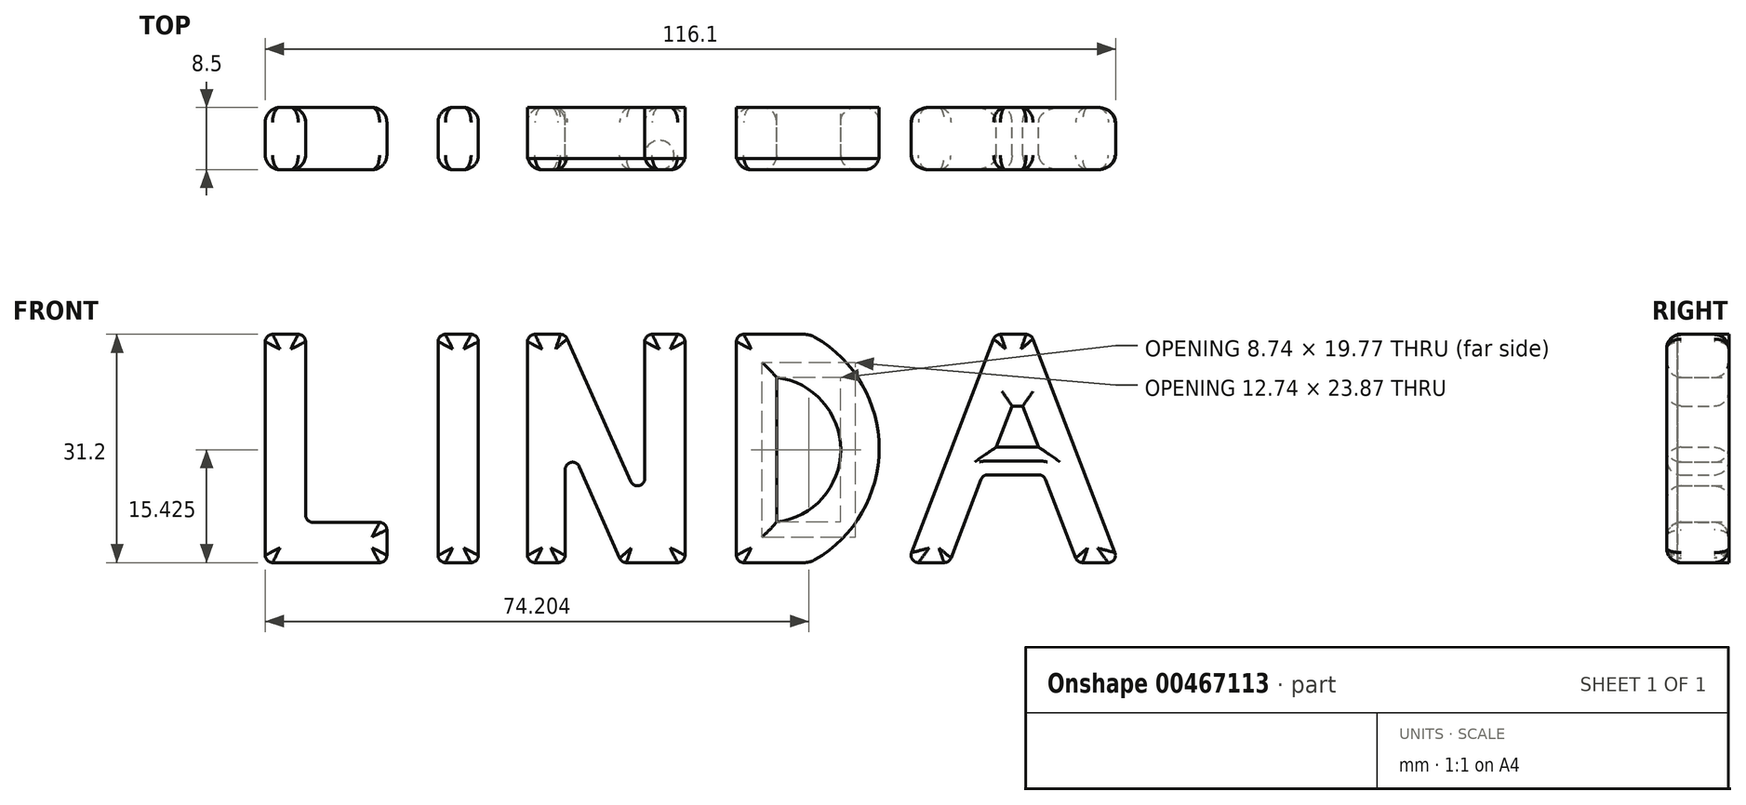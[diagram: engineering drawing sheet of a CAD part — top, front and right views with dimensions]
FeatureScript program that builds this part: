
annotation { "Feature Type Name" : "Feature", "Feature Type Description" : "" }
export const myFeature = defineFeature(function(context is Context, id is Id, definition is map)
    precondition{}
    {
        {
            var Q0;
            Q0=qCreatedBy(makeId("Front.planeOp"),FACE);
            var sketch = newSketch(context, id + "F0", { "sketchPlane" : qUnion([Q0])});
            skLineSegment(sketch, "E0", {"start": v(-68.44, 30.2) * mm, "end": v(-68.44, 1) * mm});
            skLineSegment(sketch, "E1", {"start": v(-67.44, 0) * mm, "end": v(-52.84, 0) * mm});
            skLineSegment(sketch, "E2", {"start": v(-51.84, 1) * mm, "end": v(-51.84, 4.5) * mm});
            skLineSegment(sketch, "E3", {"start": v(-52.84, 5.5) * mm, "end": v(-61.94, 5.5) * mm});
            skLineSegment(sketch, "E4", {"start": v(-62.94, 6.5) * mm, "end": v(-62.94, 30.2) * mm});
            skLineSegment(sketch, "E5", {"start": v(-63.94, 31.2) * mm, "end": v(-67.44, 31.2) * mm});
            skPoint(sketch, "E6.visualSharp", {"position": v(-62.94, 31.2) * mm});
            skArc(sketch, "E6.filletArc", {"start": v(-62.94, 30.2) * mm, "mid": v(-63.24, 30.9) * mm, "end": v(-63.94, 31.2) * mm});
            skPoint(sketch, "E7.visualSharp", {"position": v(-68.44, 31.2) * mm});
            skArc(sketch, "E7.filletArc", {"start": v(-67.44, 31.2) * mm, "mid": v(-68.15, 30.9) * mm, "end": v(-68.44, 30.2) * mm});
            skPoint(sketch, "E8.visualSharp", {"position": v(-68.44, 0) * mm});
            skArc(sketch, "E8.filletArc", {"start": v(-68.44, 1) * mm, "mid": v(-68.15, 0.3) * mm, "end": v(-67.44, 0) * mm});
            skPoint(sketch, "E9.visualSharp", {"position": v(-62.94, 5.5) * mm});
            skArc(sketch, "E9.filletArc", {"start": v(-62.94, 6.5) * mm, "mid": v(-62.65, 5.8) * mm, "end": v(-61.94, 5.5) * mm});
            skPoint(sketch, "E10.visualSharp", {"position": v(-51.84, 5.5) * mm});
            skArc(sketch, "E10.filletArc", {"start": v(-51.84, 4.5) * mm, "mid": v(-52.13, 5.2) * mm, "end": v(-52.84, 5.5) * mm});
            skPoint(sketch, "E11.visualSharp", {"position": v(-51.84, 0) * mm});
            skArc(sketch, "E11.filletArc", {"start": v(-52.84, 0) * mm, "mid": v(-52.13, 0.3) * mm, "end": v(-51.84, 1) * mm});
            skLineSegment(sketch, "E12", {"start": v(19.81, 1.36) * mm, "end": v(31.02, 30.55) * mm});
            skLineSegment(sketch, "E13", {"start": v(31.95, 31.2) * mm, "end": v(35.45, 31.2) * mm});
            skLineSegment(sketch, "E14", {"start": v(36.39, 30.55) * mm, "end": v(47.6, 1.36) * mm});
            skLineSegment(sketch, "E15", {"start": v(46.66, 0) * mm, "end": v(43.16, 0) * mm});
            skLineSegment(sketch, "E16", {"start": v(42.23, 0.64) * mm, "end": v(38.11, 11.36) * mm});
            skLineSegment(sketch, "E17", {"start": v(37.18, 12) * mm, "end": v(30.23, 12) * mm});
            skLineSegment(sketch, "E18", {"start": v(29.3, 11.36) * mm, "end": v(25.18, 0.64) * mm});
            skLineSegment(sketch, "E19", {"start": v(24.25, 0) * mm, "end": v(20.75, 0) * mm});
            skPoint(sketch, "E20.visualSharp", {"position": v(31.27, 31.2) * mm});
            skArc(sketch, "E20.filletArc", {"start": v(31.95, 31.2) * mm, "mid": v(31.39, 31.02) * mm, "end": v(31.02, 30.55) * mm});
            skPoint(sketch, "E21.visualSharp", {"position": v(19.3, 0) * mm});
            skArc(sketch, "E21.filletArc", {"start": v(19.81, 1.36) * mm, "mid": v(19.92, 0.43) * mm, "end": v(20.75, 0) * mm});
            skPoint(sketch, "E22.visualSharp", {"position": v(24.94, 0) * mm});
            skArc(sketch, "E22.filletArc", {"start": v(24.25, 0) * mm, "mid": v(24.81, 0.18) * mm, "end": v(25.18, 0.64) * mm});
            skPoint(sketch, "E23.visualSharp", {"position": v(29.54, 12) * mm});
            skArc(sketch, "E23.filletArc", {"start": v(30.23, 12) * mm, "mid": v(29.66, 11.83) * mm, "end": v(29.3, 11.36) * mm});
            skPoint(sketch, "E24.visualSharp", {"position": v(37.87, 12) * mm});
            skArc(sketch, "E24.filletArc", {"start": v(38.11, 11.36) * mm, "mid": v(37.75, 11.83) * mm, "end": v(37.18, 12) * mm});
            skPoint(sketch, "E25.visualSharp", {"position": v(42.47, 0) * mm});
            skArc(sketch, "E25.filletArc", {"start": v(42.23, 0.64) * mm, "mid": v(42.6, 0.18) * mm, "end": v(43.16, 0) * mm});
            skPoint(sketch, "E26.visualSharp", {"position": v(48.12, 0) * mm});
            skArc(sketch, "E26.filletArc", {"start": v(46.66, 0) * mm, "mid": v(47.49, 0.43) * mm, "end": v(47.6, 1.36) * mm});
            skPoint(sketch, "E27.visualSharp", {"position": v(36.14, 31.2) * mm});
            skArc(sketch, "E27.filletArc", {"start": v(36.39, 30.55) * mm, "mid": v(36.02, 31.02) * mm, "end": v(35.45, 31.2) * mm});
            skLineSegment(sketch, "E28", {"start": v(31.36, 15.77) * mm, "end": v(33.53, 21.4) * mm});
            skLineSegment(sketch, "E29", {"start": v(33.53, 21.4) * mm, "end": v(35.02, 21.4) * mm});
            skLineSegment(sketch, "E30", {"start": v(35.02, 21.4) * mm, "end": v(37.18, 15.77) * mm});
            skLineSegment(sketch, "E31", {"start": v(37.18, 15.77) * mm, "end": v(31.36, 15.77) * mm});
            skLineSegment(sketch, "E32", {"start": v(-43.84, 0) * mm, "end": v(-40.34, 0) * mm});
            skLineSegment(sketch, "E33", {"start": v(-39.34, 1) * mm, "end": v(-39.34, 30.2) * mm});
            skLineSegment(sketch, "E34", {"start": v(-40.34, 31.2) * mm, "end": v(-43.84, 31.2) * mm});
            skLineSegment(sketch, "E35", {"start": v(-44.84, 30.2) * mm, "end": v(-44.84, 1) * mm});
            skLineSegment(sketch, "E36", {"start": v(-31.63, 0) * mm, "end": v(-28.48, 0) * mm});
            skLineSegment(sketch, "E37", {"start": v(-32.63, 1) * mm, "end": v(-32.63, 30.2) * mm});
            skLineSegment(sketch, "E38", {"start": v(-31.63, 31.2) * mm, "end": v(-28.13, 31.2) * mm});
            skLineSegment(sketch, "E39", {"start": v(-27.22, 30.6) * mm, "end": v(-18.54, 11.1) * mm});
            skLineSegment(sketch, "E40", {"start": v(-27.48, 1) * mm, "end": v(-27.48, 12.73) * mm});
            skLineSegment(sketch, "E41", {"start": v(-25.57, 13.13) * mm, "end": v(-20.04, 0.6) * mm});
            skLineSegment(sketch, "E42", {"start": v(-19.13, 0) * mm, "end": v(-12.13, 0) * mm});
            skLineSegment(sketch, "E43", {"start": v(-11.13, 1) * mm, "end": v(-11.13, 30.2) * mm});
            skLineSegment(sketch, "E44", {"start": v(-12.13, 31.2) * mm, "end": v(-15.63, 31.2) * mm});
            skLineSegment(sketch, "E45", {"start": v(-16.63, 30.2) * mm, "end": v(-16.63, 11.5) * mm});
            skPoint(sketch, "E46.visualSharp", {"position": v(-32.63, 31.2) * mm});
            skArc(sketch, "E46.filletArc", {"start": v(-31.63, 31.2) * mm, "mid": v(-32.34, 30.9) * mm, "end": v(-32.63, 30.2) * mm});
            skPoint(sketch, "E47.visualSharp", {"position": v(-27.48, 31.2) * mm});
            skArc(sketch, "E47.filletArc", {"start": v(-27.22, 30.6) * mm, "mid": v(-27.59, 31.03) * mm, "end": v(-28.13, 31.2) * mm});
            skPoint(sketch, "E48.visualSharp", {"position": v(-16.63, 6.79) * mm});
            skArc(sketch, "E48.filletArc", {"start": v(-18.54, 11.1) * mm, "mid": v(-17.42, 10.52) * mm, "end": v(-16.63, 11.5) * mm});
            skPoint(sketch, "E49.visualSharp", {"position": v(-27.48, 17.47) * mm});
            skArc(sketch, "E49.filletArc", {"start": v(-25.57, 13.13) * mm, "mid": v(-26.69, 13.7) * mm, "end": v(-27.48, 12.73) * mm});
            skPoint(sketch, "E50.visualSharp", {"position": v(-16.63, 31.2) * mm});
            skArc(sketch, "E50.filletArc", {"start": v(-15.63, 31.2) * mm, "mid": v(-16.33, 30.9) * mm, "end": v(-16.63, 30.2) * mm});
            skPoint(sketch, "E51.visualSharp", {"position": v(-11.13, 31.2) * mm});
            skArc(sketch, "E51.filletArc", {"start": v(-11.13, 30.2) * mm, "mid": v(-11.42, 30.9) * mm, "end": v(-12.13, 31.2) * mm});
            skPoint(sketch, "E52.visualSharp", {"position": v(-11.13, 0) * mm});
            skArc(sketch, "E52.filletArc", {"start": v(-12.13, 0) * mm, "mid": v(-11.42, 0.3) * mm, "end": v(-11.13, 1) * mm});
            skPoint(sketch, "E53.visualSharp", {"position": v(-19.78, 0) * mm});
            skArc(sketch, "E53.filletArc", {"start": v(-20.04, 0.6) * mm, "mid": v(-19.67, 0.16) * mm, "end": v(-19.13, 0) * mm});
            skPoint(sketch, "E54.visualSharp", {"position": v(-27.48, 0) * mm});
            skArc(sketch, "E54.filletArc", {"start": v(-28.48, 0) * mm, "mid": v(-27.78, 0.3) * mm, "end": v(-27.48, 1) * mm});
            skPoint(sketch, "E55.visualSharp", {"position": v(-32.63, 0) * mm});
            skArc(sketch, "E55.filletArc", {"start": v(-32.63, 1) * mm, "mid": v(-32.34, 0.3) * mm, "end": v(-31.63, 0) * mm});
            skPoint(sketch, "E56.visualSharp", {"position": v(-39.34, 0) * mm});
            skArc(sketch, "E56.filletArc", {"start": v(-40.34, 0) * mm, "mid": v(-39.63, 0.3) * mm, "end": v(-39.34, 1) * mm});
            skPoint(sketch, "E57.visualSharp", {"position": v(-39.34, 31.2) * mm});
            skArc(sketch, "E57.filletArc", {"start": v(-39.34, 30.2) * mm, "mid": v(-39.63, 30.9) * mm, "end": v(-40.34, 31.2) * mm});
            skPoint(sketch, "E58.visualSharp", {"position": v(-44.84, 31.2) * mm});
            skArc(sketch, "E58.filletArc", {"start": v(-43.84, 31.2) * mm, "mid": v(-44.55, 30.9) * mm, "end": v(-44.84, 30.2) * mm});
            skPoint(sketch, "E59.visualSharp", {"position": v(-44.84, 0) * mm});
            skArc(sketch, "E59.filletArc", {"start": v(-44.84, 1) * mm, "mid": v(-44.55, 0.3) * mm, "end": v(-43.84, 0) * mm});
            skLineSegment(sketch, "E60", {"start": v(-3.1, 0) * mm, "end": v(5.13, 0) * mm});
            skLineSegment(sketch, "E61", {"start": v(-4.1, 1) * mm, "end": v(-4.1, 30.2) * mm});
            skLineSegment(sketch, "E62", {"start": v(-3.1, 31.2) * mm, "end": v(5.13, 31.2) * mm});
            skArc(sketch, "E63", {"start": v(6.64, 0.4) * mm, "mid": v(15.38, 15.6) * mm, "end": v(6.64, 30.8) * mm});
            skLineSegment(sketch, "E64", {"start": v(1.4, 25.3) * mm, "end": v(1.4, 5.54) * mm});
            skArc(sketch, "E65", {"start": v(1.4, 5.54) * mm, "mid": v(10.13, 15.43) * mm, "end": v(1.4, 25.3) * mm});
            skPoint(sketch, "E66.visualSharp", {"position": v(-4.1, 31.2) * mm});
            skArc(sketch, "E66.filletArc", {"start": v(-3.1, 31.2) * mm, "mid": v(-3.81, 30.9) * mm, "end": v(-4.1, 30.2) * mm});
            skPoint(sketch, "E67.visualSharp", {"position": v(-4.1, 0) * mm});
            skArc(sketch, "E67.filletArc", {"start": v(-4.1, 1) * mm, "mid": v(-3.81, 0.3) * mm, "end": v(-3.1, 0) * mm});
            skPoint(sketch, "E68.visualSharp", {"position": v(5.9, 31.2) * mm});
            skArc(sketch, "E68.filletArc", {"start": v(6.64, 30.8) * mm, "mid": v(5.9, 31.1) * mm, "end": v(5.13, 31.2) * mm});
            skPoint(sketch, "E69.visualSharp", {"position": v(5.9, 0) * mm});
            skArc(sketch, "E69.filletArc", {"start": v(5.13, 0) * mm, "mid": v(5.9, 0.1) * mm, "end": v(6.64, 0.4) * mm});
            skSolve(sketch);
        }
        {
            var Q0;
            Q0 = qSketchRegion(id + "F0", true);
            extrude(context, id + "F1", {"entities" : qUnion([Q0]), "depth" : 8.5 * mm});
        }
        {
            var Q0;
            Q0=makeQuery(id+"F1.opExtrude","CAP_FACE",FACE,{"disambiguationData":[OSD([sQuery(id+"F0.wireOp",EDGE,"E0"),sQuery(id+"F0.wireOp",EDGE,"E1"),sQuery(id+"F0.wireOp",EDGE,"E2"),sQuery(id+"F0.wireOp",EDGE,"E3"),sQuery(id+"F0.wireOp",EDGE,"E4"),sQuery(id+"F0.wireOp",EDGE,"E5"),sQuery(id+"F0.wireOp",EDGE,"E6.filletArc"),sQuery(id+"F0.wireOp",EDGE,"E7.filletArc"),sQuery(id+"F0.wireOp",EDGE,"E8.filletArc"),sQuery(id+"F0.wireOp",EDGE,"E9.filletArc"),sQuery(id+"F0.wireOp",EDGE,"E10.filletArc"),sQuery(id+"F0.wireOp",EDGE,"E11.filletArc")])],"isStart":false});
            var Q1;
            Q1=makeQuery(id+"F1.opExtrude","CAP_FACE",FACE,{"disambiguationData":[OSD([sQuery(id+"F0.wireOp",EDGE,"E0"),sQuery(id+"F0.wireOp",EDGE,"E1"),sQuery(id+"F0.wireOp",EDGE,"E2"),sQuery(id+"F0.wireOp",EDGE,"E3"),sQuery(id+"F0.wireOp",EDGE,"E4"),sQuery(id+"F0.wireOp",EDGE,"E5"),sQuery(id+"F0.wireOp",EDGE,"E6.filletArc"),sQuery(id+"F0.wireOp",EDGE,"E7.filletArc"),sQuery(id+"F0.wireOp",EDGE,"E8.filletArc"),sQuery(id+"F0.wireOp",EDGE,"E9.filletArc"),sQuery(id+"F0.wireOp",EDGE,"E10.filletArc"),sQuery(id+"F0.wireOp",EDGE,"E11.filletArc")])],"isStart":true});
            fillet(context, id + "F2", {"entities" : qUnion([Q0, Q1]), "radius" : 2 * mm, "tangentPropagation" : true, "allowEdgeOverflow" : false});
        }
        {
            var Q0;
            Q0=makeQuery(id+"F0.imprint","IMPRINT",FACE,{"disambiguationData":[TD([[makeQuery(id+"F0.imprint","IMPRINT",EDGE,{"derivedFrom":sQuery(id+"F0.wireOp",EDGE,"E12")}),-1.0]])]});
            extrude(context, id + "F3", {"entities" : qUnion([Q0]), "operationType" : NewBodyOperationType.ADD, "depth" : 7 * mm});
        }
        {
            var Q0;
            Q0=makeQuery(id+"F1.opExtrude","CAP_FACE",FACE,{"disambiguationData":[OSD([sQuery(id+"F0.wireOp",EDGE,"E12"),sQuery(id+"F0.wireOp",EDGE,"E13"),sQuery(id+"F0.wireOp",EDGE,"E14"),sQuery(id+"F0.wireOp",EDGE,"E15"),sQuery(id+"F0.wireOp",EDGE,"E16"),sQuery(id+"F0.wireOp",EDGE,"E17"),sQuery(id+"F0.wireOp",EDGE,"E18"),sQuery(id+"F0.wireOp",EDGE,"E19"),sQuery(id+"F0.wireOp",EDGE,"E20.filletArc"),sQuery(id+"F0.wireOp",EDGE,"E21.filletArc"),sQuery(id+"F0.wireOp",EDGE,"E22.filletArc"),sQuery(id+"F0.wireOp",EDGE,"E23.filletArc"),sQuery(id+"F0.wireOp",EDGE,"E24.filletArc"),sQuery(id+"F0.wireOp",EDGE,"E25.filletArc"),sQuery(id+"F0.wireOp",EDGE,"E26.filletArc"),sQuery(id+"F0.wireOp",EDGE,"E27.filletArc"),sQuery(id+"F0.wireOp",EDGE,"E28"),sQuery(id+"F0.wireOp",EDGE,"E29"),sQuery(id+"F0.wireOp",EDGE,"E30"),sQuery(id+"F0.wireOp",EDGE,"E31")])],"isStart":false});
            var Q1;
            Q1=makeQuery(id+"F1.opExtrude","CAP_FACE",FACE,{"disambiguationData":[OSD([sQuery(id+"F0.wireOp",EDGE,"E12"),sQuery(id+"F0.wireOp",EDGE,"E13"),sQuery(id+"F0.wireOp",EDGE,"E14"),sQuery(id+"F0.wireOp",EDGE,"E15"),sQuery(id+"F0.wireOp",EDGE,"E16"),sQuery(id+"F0.wireOp",EDGE,"E17"),sQuery(id+"F0.wireOp",EDGE,"E18"),sQuery(id+"F0.wireOp",EDGE,"E19"),sQuery(id+"F0.wireOp",EDGE,"E20.filletArc"),sQuery(id+"F0.wireOp",EDGE,"E21.filletArc"),sQuery(id+"F0.wireOp",EDGE,"E22.filletArc"),sQuery(id+"F0.wireOp",EDGE,"E23.filletArc"),sQuery(id+"F0.wireOp",EDGE,"E24.filletArc"),sQuery(id+"F0.wireOp",EDGE,"E25.filletArc"),sQuery(id+"F0.wireOp",EDGE,"E26.filletArc"),sQuery(id+"F0.wireOp",EDGE,"E27.filletArc"),sQuery(id+"F0.wireOp",EDGE,"E28"),sQuery(id+"F0.wireOp",EDGE,"E29"),sQuery(id+"F0.wireOp",EDGE,"E30"),sQuery(id+"F0.wireOp",EDGE,"E31")])],"isStart":true});
            fillet(context, id + "F4", {"entities" : qUnion([Q0, Q1]), "radius" : 2 * mm, "tangentPropagation" : true, "allowEdgeOverflow" : false});
        }
        {
            var Q0;
            Q0=makeQuery(id+"F0.imprint","IMPRINT",FACE,{"disambiguationData":[TD([[makeQuery(id+"F0.imprint","IMPRINT",EDGE,{"derivedFrom":sQuery(id+"F0.wireOp",EDGE,"E36")}),1.0]])]});
            var Q1;
            Q1=makeQuery(id+"F0.imprint","IMPRINT",FACE,{"disambiguationData":[TD([[makeQuery(id+"F0.imprint","IMPRINT",EDGE,{"derivedFrom":sQuery(id+"F0.wireOp",EDGE,"E60")}),1.0]])]});
            extrude(context, id + "F5", {"entities" : qUnion([Q0, Q1]), "depth" : 7 * mm});
        }
        {
            var Q0;
            Q0=makeQuery(id+"F1.opExtrude","CAP_FACE",FACE,{"disambiguationData":[OSD([sQuery(id+"F0.wireOp",EDGE,"E36"),sQuery(id+"F0.wireOp",EDGE,"E37"),sQuery(id+"F0.wireOp",EDGE,"E38"),sQuery(id+"F0.wireOp",EDGE,"E39"),sQuery(id+"F0.wireOp",EDGE,"E40"),sQuery(id+"F0.wireOp",EDGE,"E41"),sQuery(id+"F0.wireOp",EDGE,"E42"),sQuery(id+"F0.wireOp",EDGE,"E43"),sQuery(id+"F0.wireOp",EDGE,"E44"),sQuery(id+"F0.wireOp",EDGE,"E45"),sQuery(id+"F0.wireOp",EDGE,"E46.filletArc"),sQuery(id+"F0.wireOp",EDGE,"E47.filletArc"),sQuery(id+"F0.wireOp",EDGE,"E48.filletArc"),sQuery(id+"F0.wireOp",EDGE,"E49.filletArc"),sQuery(id+"F0.wireOp",EDGE,"E50.filletArc"),sQuery(id+"F0.wireOp",EDGE,"E51.filletArc"),sQuery(id+"F0.wireOp",EDGE,"E52.filletArc"),sQuery(id+"F0.wireOp",EDGE,"E53.filletArc"),sQuery(id+"F0.wireOp",EDGE,"E54.filletArc"),sQuery(id+"F0.wireOp",EDGE,"E55.filletArc")])],"isStart":false});
            var Q1;
            Q1=makeQuery(id+"F1.opExtrude","CAP_FACE",FACE,{"disambiguationData":[OSD([sQuery(id+"F0.wireOp",EDGE,"E60"),sQuery(id+"F0.wireOp",EDGE,"E61"),sQuery(id+"F0.wireOp",EDGE,"E62"),sQuery(id+"F0.wireOp",EDGE,"E63"),sQuery(id+"F0.wireOp",EDGE,"E64"),sQuery(id+"F0.wireOp",EDGE,"E65"),sQuery(id+"F0.wireOp",EDGE,"E66.filletArc"),sQuery(id+"F0.wireOp",EDGE,"E67.filletArc"),sQuery(id+"F0.wireOp",EDGE,"E68.filletArc"),sQuery(id+"F0.wireOp",EDGE,"E69.filletArc")])],"isStart":false});
            var Q2;
            Q2=makeQuery(id+"F1.opExtrude","CAP_FACE",FACE,{"disambiguationData":[OSD([sQuery(id+"F0.wireOp",EDGE,"E32"),sQuery(id+"F0.wireOp",EDGE,"E33"),sQuery(id+"F0.wireOp",EDGE,"E34"),sQuery(id+"F0.wireOp",EDGE,"E35"),sQuery(id+"F0.wireOp",EDGE,"E56.filletArc"),sQuery(id+"F0.wireOp",EDGE,"E57.filletArc"),sQuery(id+"F0.wireOp",EDGE,"E58.filletArc"),sQuery(id+"F0.wireOp",EDGE,"E59.filletArc")])],"isStart":false});
            var Q3;
            Q3=makeQuery(id+"F1.opExtrude","CAP_FACE",FACE,{"disambiguationData":[OSD([sQuery(id+"F0.wireOp",EDGE,"E32"),sQuery(id+"F0.wireOp",EDGE,"E33"),sQuery(id+"F0.wireOp",EDGE,"E34"),sQuery(id+"F0.wireOp",EDGE,"E35"),sQuery(id+"F0.wireOp",EDGE,"E56.filletArc"),sQuery(id+"F0.wireOp",EDGE,"E57.filletArc"),sQuery(id+"F0.wireOp",EDGE,"E58.filletArc"),sQuery(id+"F0.wireOp",EDGE,"E59.filletArc")])],"isStart":true});
            var Q4;
            Q4=makeQuery(id+"F1.opExtrude","CAP_FACE",FACE,{"disambiguationData":[OSD([sQuery(id+"F0.wireOp",EDGE,"E36"),sQuery(id+"F0.wireOp",EDGE,"E37"),sQuery(id+"F0.wireOp",EDGE,"E38"),sQuery(id+"F0.wireOp",EDGE,"E39"),sQuery(id+"F0.wireOp",EDGE,"E40"),sQuery(id+"F0.wireOp",EDGE,"E41"),sQuery(id+"F0.wireOp",EDGE,"E42"),sQuery(id+"F0.wireOp",EDGE,"E43"),sQuery(id+"F0.wireOp",EDGE,"E44"),sQuery(id+"F0.wireOp",EDGE,"E45"),sQuery(id+"F0.wireOp",EDGE,"E46.filletArc"),sQuery(id+"F0.wireOp",EDGE,"E47.filletArc"),sQuery(id+"F0.wireOp",EDGE,"E48.filletArc"),sQuery(id+"F0.wireOp",EDGE,"E49.filletArc"),sQuery(id+"F0.wireOp",EDGE,"E50.filletArc"),sQuery(id+"F0.wireOp",EDGE,"E51.filletArc"),sQuery(id+"F0.wireOp",EDGE,"E52.filletArc"),sQuery(id+"F0.wireOp",EDGE,"E53.filletArc"),sQuery(id+"F0.wireOp",EDGE,"E54.filletArc"),sQuery(id+"F0.wireOp",EDGE,"E55.filletArc")])],"isStart":true});
            var Q5;
            Q5=makeQuery(id+"F1.opExtrude","CAP_FACE",FACE,{"disambiguationData":[OSD([sQuery(id+"F0.wireOp",EDGE,"E60"),sQuery(id+"F0.wireOp",EDGE,"E61"),sQuery(id+"F0.wireOp",EDGE,"E62"),sQuery(id+"F0.wireOp",EDGE,"E63"),sQuery(id+"F0.wireOp",EDGE,"E64"),sQuery(id+"F0.wireOp",EDGE,"E65"),sQuery(id+"F0.wireOp",EDGE,"E66.filletArc"),sQuery(id+"F0.wireOp",EDGE,"E67.filletArc"),sQuery(id+"F0.wireOp",EDGE,"E68.filletArc"),sQuery(id+"F0.wireOp",EDGE,"E69.filletArc")])],"isStart":true});
            fillet(context, id + "F6", {"entities" : qUnion([Q0, Q1, Q2, Q3, Q4, Q5]), "radius" : 2 * mm, "tangentPropagation" : true, "allowEdgeOverflow" : false});
        }
    });
